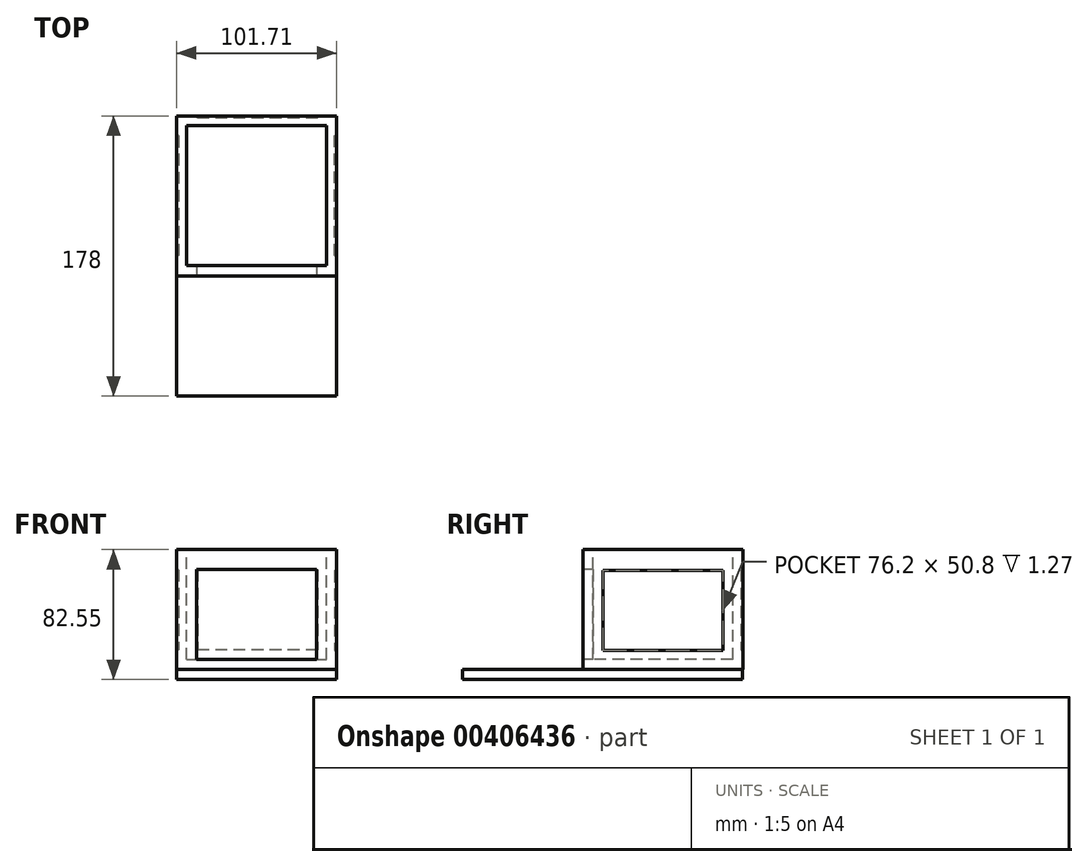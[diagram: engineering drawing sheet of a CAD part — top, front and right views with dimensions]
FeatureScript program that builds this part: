
annotation { "Feature Type Name" : "Feature", "Feature Type Description" : "" }
export const myFeature = defineFeature(function(context is Context, id is Id, definition is map)
    precondition{}
    {
        {
            var Q0;
            Q0=qCreatedBy(makeId("Top.planeOp"),FACE);
            var sketch = newSketch(context, id + "F0", { "sketchPlane" : qUnion([Q0])});
            skLineSegment(sketch, "E0.bottom", {"start": v(-45.9, 50.56) * mm, "end": v(55.7, 50.56) * mm});
            skLineSegment(sketch, "E0.top", {"start": v(-45.9, -51.04) * mm, "end": v(55.7, -51.04) * mm});
            skLineSegment(sketch, "E0.left", {"start": v(-45.9, 50.56) * mm, "end": v(-45.9, -51.04) * mm});
            skLineSegment(sketch, "E0.right", {"start": v(55.7, 50.56) * mm, "end": v(55.7, -51.04) * mm});
            skSolve(sketch);
        }
        {
            var Q0;
            Q0=makeQuery(id+"F0.imprint","IMPRINT",FACE,{"disambiguationData":[TD([[makeQuery(id+"F0.imprint","IMPRINT",EDGE,{"derivedFrom":sQuery(id+"F0.wireOp",EDGE,"E0.bottom")}),-1.0]])]});
            extrude(context, id + "F1", {"entities" : qUnion([Q0]), "depth" : 76.2 * mm});
        }
        {
            var Q0;
            Q0=makeQuery(id+"F1.opExtrude","CAP_FACE",FACE,{"disambiguationData":[OSD([sQuery(id+"F0.wireOp",EDGE,"E0.bottom"),sQuery(id+"F0.wireOp",EDGE,"E0.top"),sQuery(id+"F0.wireOp",EDGE,"E0.left"),sQuery(id+"F0.wireOp",EDGE,"E0.right")])],"isStart":false});
            var sketch = newSketch(context, id + "F2", { "sketchPlane" : qUnion([Q0])});
            skLineSegment(sketch, "E1.bottom", {"start": v(-39.64, 44.29) * mm, "end": v(49.26, 44.29) * mm});
            skLineSegment(sketch, "E1.top", {"start": v(-39.64, -44.61) * mm, "end": v(49.26, -44.61) * mm});
            skLineSegment(sketch, "E1.left", {"start": v(-39.64, 44.29) * mm, "end": v(-39.64, -44.61) * mm});
            skLineSegment(sketch, "E1.right", {"start": v(49.26, 44.29) * mm, "end": v(49.26, -44.61) * mm});
            skSolve(sketch);
        }
        {
            var Q0;
            Q0=makeQuery(id+"F2.imprint","IMPRINT",FACE,{"disambiguationData":[TD([[makeQuery(id+"F2.imprint","IMPRINT",EDGE,{"derivedFrom":sQuery(id+"F2.wireOp",EDGE,"E1.bottom")}),-1.0]])]});
            extrude(context, id + "F3", {"entities" : qUnion([Q0]), "operationType" : NewBodyOperationType.REMOVE, "oppositeDirection" : true, "depth" : 69.85 * mm});
        }
        {
            var Q0;
            Q0=makeQuery(id+"F1.opExtrude","SWEPT_FACE",FACE,{"disambiguationData":[OSD([sQuery(id+"F0.wireOp",EDGE,"E0.top")])]});
            var sketch = newSketch(context, id + "F4", { "sketchPlane" : qUnion([Q0])});
            skPoint(sketch, "E2.top.start.orphan", {"position": v(-33.3, 0) * mm});
            skLineSegment(sketch, "E3.bottom", {"start": v(-33.03, 63.5) * mm, "end": v(43.17, 63.5) * mm});
            skLineSegment(sketch, "E3.top", {"start": v(-33.03, 6.35) * mm, "end": v(43.17, 6.35) * mm});
            skLineSegment(sketch, "E3.left", {"start": v(-33.03, 63.5) * mm, "end": v(-33.03, 6.35) * mm});
            skLineSegment(sketch, "E3.right", {"start": v(43.17, 63.5) * mm, "end": v(43.17, 6.35) * mm});
            skLineSegment(sketch, "E4", {"start": v(26.43, 6.35) * mm, "end": v(26.43, 0) * mm, "construction": true});
            skSolve(sketch);
        }
        {
            var Q0;
            Q0=makeQuery(id+"F4.imprint","IMPRINT",FACE,{"disambiguationData":[TD([[makeQuery(id+"F4.imprint","IMPRINT",EDGE,{"derivedFrom":sQuery(id+"F4.wireOp",EDGE,"E3.bottom")}),-1.0]])]});
            extrude(context, id + "F5", {"entities" : qUnion([Q0]), "operationType" : NewBodyOperationType.REMOVE, "oppositeDirection" : true, "depth" : 12.7 * mm});
        }
        {
            var Q0;
            Q0=makeQuery(id+"F1.opExtrude","SWEPT_FACE",FACE,{"disambiguationData":[OSD([sQuery(id+"F0.wireOp",EDGE,"E0.left")])]});
            var sketch = newSketch(context, id + "F6", { "sketchPlane" : qUnion([Q0])});
            skLineSegment(sketch, "E5.bottom", {"start": v(-38.03, 63.45) * mm, "end": v(38.17, 63.45) * mm});
            skLineSegment(sketch, "E5.top", {"start": v(-38.03, 12.65) * mm, "end": v(38.17, 12.65) * mm});
            skLineSegment(sketch, "E5.left", {"start": v(-38.03, 63.45) * mm, "end": v(-38.03, 12.65) * mm});
            skLineSegment(sketch, "E5.right", {"start": v(38.17, 63.45) * mm, "end": v(38.17, 12.65) * mm});
            skSolve(sketch);
        }
        {
            var Q0;
            Q0=makeQuery(id+"F6.imprint","IMPRINT",FACE,{"disambiguationData":[TD([[makeQuery(id+"F6.imprint","IMPRINT",EDGE,{"derivedFrom":sQuery(id+"F6.wireOp",EDGE,"E5.bottom")}),-1.0]])]});
            extrude(context, id + "F7", {"entities" : qUnion([Q0]), "operationType" : NewBodyOperationType.REMOVE, "oppositeDirection" : true, "depth" : 1.27 * mm});
        }
        {
            var Q0;
            Q0=makeQuery(id+"F1.opExtrude","SWEPT_FACE",FACE,{"disambiguationData":[OSD([sQuery(id+"F0.wireOp",EDGE,"E0.bottom")])]});
            var sketch = newSketch(context, id + "F8", { "sketchPlane" : qUnion([Q0])});
            skLineSegment(sketch, "E6.bottom", {"start": v(-43.8, 63.45) * mm, "end": v(32.4, 63.45) * mm});
            skLineSegment(sketch, "E6.top", {"start": v(-43.8, 12.65) * mm, "end": v(32.4, 12.65) * mm});
            skLineSegment(sketch, "E6.left", {"start": v(-43.8, 63.45) * mm, "end": v(-43.8, 12.65) * mm});
            skLineSegment(sketch, "E6.right", {"start": v(32.4, 63.45) * mm, "end": v(32.4, 12.65) * mm});
            skSolve(sketch);
        }
        {
            var Q0;
            Q0=makeQuery(id+"F8.imprint","IMPRINT",FACE,{"disambiguationData":[TD([[makeQuery(id+"F8.imprint","IMPRINT",EDGE,{"derivedFrom":sQuery(id+"F8.wireOp",EDGE,"E6.bottom")}),-1.0]])]});
            extrude(context, id + "F9", {"entities" : qUnion([Q0]), "operationType" : NewBodyOperationType.REMOVE, "oppositeDirection" : true, "depth" : 1.27 * mm});
        }
        {
            var Q0;
            Q0=makeQuery(id+"F1.opExtrude","SWEPT_FACE",FACE,{"disambiguationData":[OSD([sQuery(id+"F0.wireOp",EDGE,"E0.right")])]});
            var sketch = newSketch(context, id + "F10", { "sketchPlane" : qUnion([Q0])});
            skLineSegment(sketch, "E7.bottom", {"start": v(-38.25, 62.97) * mm, "end": v(37.95, 62.97) * mm});
            skLineSegment(sketch, "E7.top", {"start": v(-38.25, 12.17) * mm, "end": v(37.95, 12.17) * mm});
            skLineSegment(sketch, "E7.left", {"start": v(-38.25, 62.97) * mm, "end": v(-38.25, 12.17) * mm});
            skLineSegment(sketch, "E7.right", {"start": v(37.95, 62.97) * mm, "end": v(37.95, 12.17) * mm});
            skSolve(sketch);
        }
        {
            var Q0;
            Q0=makeQuery(id+"F10.imprint","IMPRINT",FACE,{"disambiguationData":[TD([[makeQuery(id+"F10.imprint","IMPRINT",EDGE,{"derivedFrom":sQuery(id+"F10.wireOp",EDGE,"E7.bottom")}),-1.0]])]});
            extrude(context, id + "F11", {"entities" : qUnion([Q0]), "operationType" : NewBodyOperationType.REMOVE, "oppositeDirection" : true, "depth" : 1.27 * mm});
        }
        {
            var Q0;
            Q0=qCreatedBy(makeId("Top.planeOp"),FACE);
            var sketch = newSketch(context, id + "F12", { "sketchPlane" : qUnion([Q0])});
            skLineSegment(sketch, "E8.bottom", {"start": v(-45.8, -127.44) * mm, "end": v(55.8, -127.44) * mm});
            skLineSegment(sketch, "E8.top", {"start": v(-45.8, 50.36) * mm, "end": v(55.8, 50.36) * mm});
            skLineSegment(sketch, "E8.left", {"start": v(-45.8, -127.44) * mm, "end": v(-45.8, 50.36) * mm});
            skLineSegment(sketch, "E8.right", {"start": v(55.8, -127.44) * mm, "end": v(55.8, 50.36) * mm});
            skSolve(sketch);
        }
        {
            var Q0;
            Q0=makeQuery(id+"F12.imprint","IMPRINT",FACE,{"disambiguationData":[TD([[makeQuery(id+"F12.imprint","IMPRINT",EDGE,{"derivedFrom":sQuery(id+"F12.wireOp",EDGE,"E8.bottom")}),1.0]])]});
            extrude(context, id + "F13", {"entities" : qUnion([Q0]), "operationType" : NewBodyOperationType.ADD, "oppositeDirection" : true, "depth" : 6.35 * mm});
        }
    });
